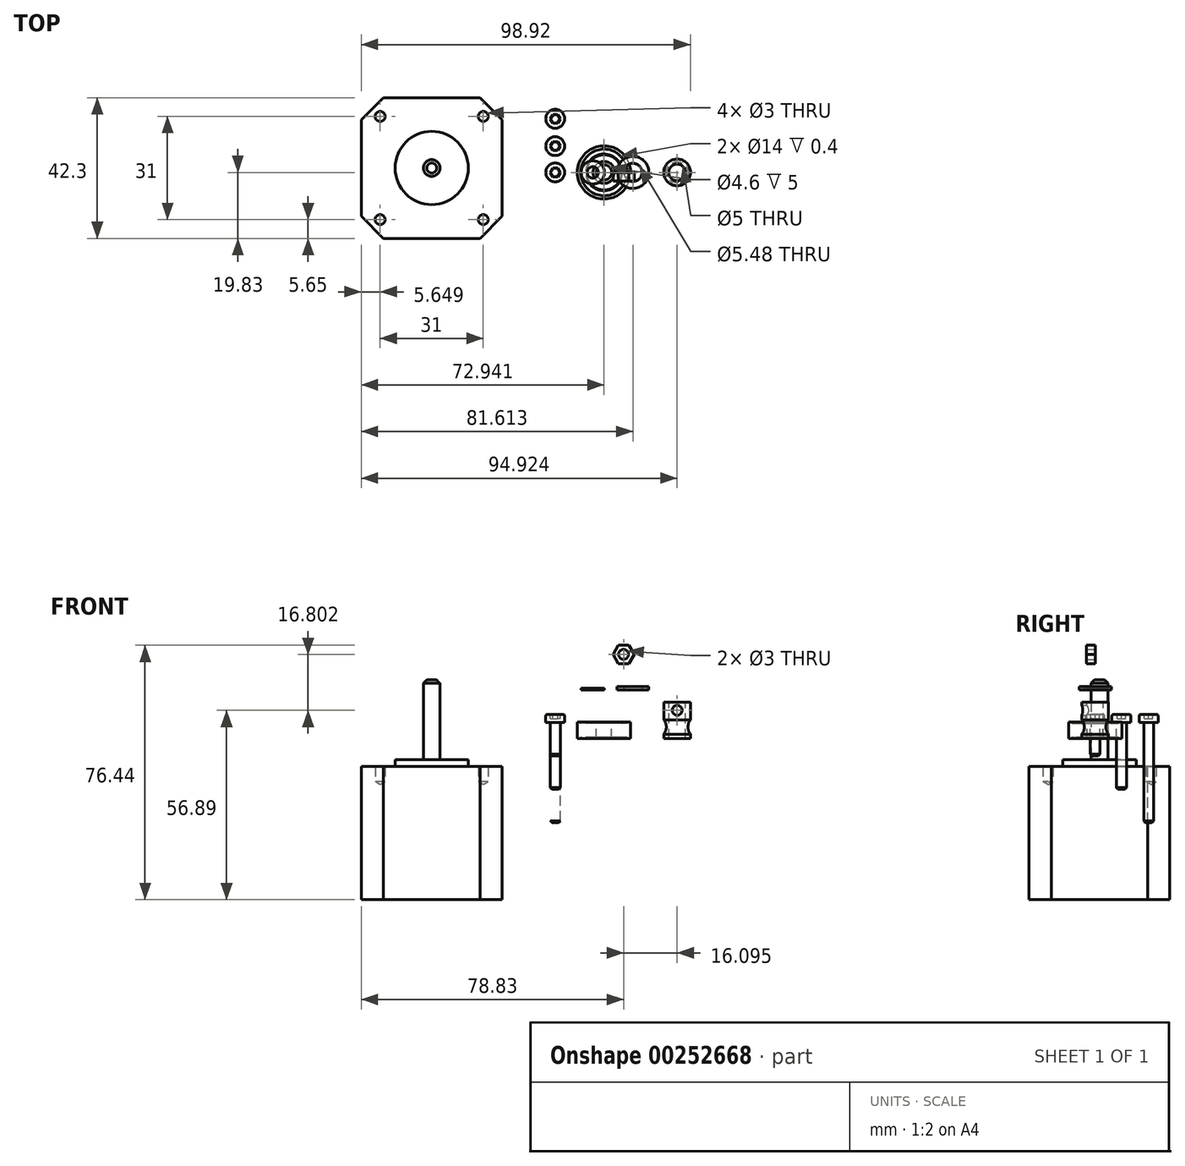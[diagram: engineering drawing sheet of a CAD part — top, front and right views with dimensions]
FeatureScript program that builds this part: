
annotation { "Feature Type Name" : "Feature", "Feature Type Description" : "" }
export const myFeature = defineFeature(function(context is Context, id is Id, definition is map)
    precondition{}
    {
        {
            var Q0;
            Q0=qCreatedBy(makeId("Front.planeOp"),FACE);
            var sketch = newSketch(context, id + "F0", { "sketchPlane" : qUnion([Q0])});
            skLineSegment(sketch, "E0.bottom", {"start": v(-24.66, 19.4) * mm, "end": v(-16.66, 19.4) * mm});
            skLineSegment(sketch, "E0.top", {"start": v(-24.66, 8.4) * mm, "end": v(-16.66, 8.4) * mm});
            skLineSegment(sketch, "E0.left", {"start": v(-24.66, 19.4) * mm, "end": v(-24.66, 8.4) * mm});
            skLineSegment(sketch, "E0.right", {"start": v(-16.66, 19.4) * mm, "end": v(-16.66, 8.4) * mm});
            skLineSegment(sketch, "E1", {"start": v(-20.66, 19.4) * mm, "end": v(-20.66, 8.4) * mm, "construction": true});
            skLineSegment(sketch, "E2", {"start": v(-23.16, 19.4) * mm, "end": v(-23.16, 8.4) * mm});
            skLineSegment(sketch, "E3", {"start": v(-18.16, 8.4) * mm, "end": v(-18.16, 19.4) * mm});
            skCircle(sketch, "E4", {"center": v(-27.4, 11.9) * mm, "radius": 3.5 * mm});
            skCircle(sketch, "E5", {"center": v(-20.66, 16.9) * mm, "radius": 1.5 * mm});
            skLineSegment(sketch, "E6", {"start": v(-34.64, 8.35) * mm, "end": v(-34.64, 13.35) * mm});
            skLineSegment(sketch, "E7", {"start": v(-34.64, 13.35) * mm, "end": v(-50.64, 13.35) * mm, "construction": true});
            skLineSegment(sketch, "E8", {"start": v(-50.64, 13.35) * mm, "end": v(-50.64, 8.35) * mm});
            skLineSegment(sketch, "E9", {"start": v(-50.64, 8.35) * mm, "end": v(-34.64, 8.35) * mm, "construction": true});
            skLineSegment(sketch, "E10", {"start": v(-44.94, 13.35) * mm, "end": v(-44.94, 8.35) * mm});
            skLineSegment(sketch, "E11", {"start": v(-39.94, 13.35) * mm, "end": v(-39.94, 8.35) * mm});
            skLineSegment(sketch, "E12", {"start": v(-42.64, 13.35) * mm, "end": v(-42.64, 8.35) * mm, "construction": true});
            skLineSegment(sketch, "E13", {"start": v(-44.94, 13.35) * mm, "end": v(-45.94, 13.35) * mm});
            skLineSegment(sketch, "E14", {"start": v(-45.94, 13.35) * mm, "end": v(-45.94, 13.15) * mm});
            skLineSegment(sketch, "E15", {"start": v(-45.94, 13.15) * mm, "end": v(-47.94, 13.15) * mm});
            skLineSegment(sketch, "E16", {"start": v(-47.94, 13.15) * mm, "end": v(-48.14, 12.95) * mm});
            skLineSegment(sketch, "E17", {"start": v(-48.14, 12.95) * mm, "end": v(-49.64, 12.95) * mm});
            skLineSegment(sketch, "E18", {"start": v(-49.64, 12.95) * mm, "end": v(-49.64, 13.35) * mm});
            skLineSegment(sketch, "E19", {"start": v(-49.64, 13.35) * mm, "end": v(-50.64, 13.35) * mm});
            skLineSegment(sketch, "E20", {"start": v(-50.64, 8.35) * mm, "end": v(-49.64, 8.35) * mm});
            skLineSegment(sketch, "E21", {"start": v(-49.64, 8.35) * mm, "end": v(-49.64, 8.75) * mm});
            skLineSegment(sketch, "E22", {"start": v(-49.64, 8.75) * mm, "end": v(-48.14, 8.75) * mm});
            skLineSegment(sketch, "E23", {"start": v(-48.14, 8.75) * mm, "end": v(-47.94, 8.55) * mm});
            skLineSegment(sketch, "E24", {"start": v(-47.94, 8.55) * mm, "end": v(-45.94, 8.55) * mm});
            skLineSegment(sketch, "E25", {"start": v(-45.94, 8.55) * mm, "end": v(-45.94, 8.35) * mm});
            skLineSegment(sketch, "E26", {"start": v(-45.94, 8.35) * mm, "end": v(-44.94, 8.35) * mm});
            skLineSegment(sketch, "E27.bottom", {"start": v(-49.5, 23.55) * mm, "end": v(-42.5, 23.55) * mm, "construction": true});
            skLineSegment(sketch, "E27.top", {"start": v(-49.5, 23.05) * mm, "end": v(-42.5, 23.05) * mm, "construction": true});
            skLineSegment(sketch, "E27.left", {"start": v(-49.5, 23.55) * mm, "end": v(-49.5, 23.05) * mm, "construction": true});
            skLineSegment(sketch, "E27.right", {"start": v(-42.5, 23.55) * mm, "end": v(-42.5, 23.05) * mm, "construction": true});
            skLineSegment(sketch, "E28", {"start": v(-46, 23.55) * mm, "end": v(-46, 23.05) * mm, "construction": true});
            skLineSegment(sketch, "E29.bottom", {"start": v(-49.5, 23.55) * mm, "end": v(-47.69, 23.55) * mm});
            skLineSegment(sketch, "E29.top", {"start": v(-49.5, 23.05) * mm, "end": v(-47.69, 23.05) * mm});
            skLineSegment(sketch, "E29.left", {"start": v(-49.5, 23.55) * mm, "end": v(-49.5, 23.05) * mm});
            skLineSegment(sketch, "E29.right", {"start": v(-47.69, 23.55) * mm, "end": v(-47.69, 23.05) * mm});
            skLineSegment(sketch, "E30", {"start": v(-60.14, 15.17) * mm, "end": v(-60.14, 13.17) * mm});
            skLineSegment(sketch, "E31", {"start": v(-60.14, 13.17) * mm, "end": v(-54.46, 13.17) * mm});
            skLineSegment(sketch, "E32", {"start": v(-54.46, 13.17) * mm, "end": v(-54.46, 15.17) * mm});
            skLineSegment(sketch, "E33", {"start": v(-54.96, 15.67) * mm, "end": v(-59.64, 15.67) * mm});
            skLineSegment(sketch, "E34", {"start": v(-57.3, 13.17) * mm, "end": v(-57.3, 3.17) * mm});
            skLineSegment(sketch, "E35", {"start": v(-58.8, 13.17) * mm, "end": v(-58.8, 3.17) * mm, "construction": true});
            skLineSegment(sketch, "E36", {"start": v(-58.8, 3.17) * mm, "end": v(-55.8, 3.17) * mm, "construction": true});
            skLineSegment(sketch, "E37", {"start": v(-55.8, 3.17) * mm, "end": v(-55.8, 13.17) * mm, "construction": true});
            skPoint(sketch, "E38.visualSharp", {"position": v(-60.14, 15.67) * mm});
            skArc(sketch, "E38.filletArc", {"start": v(-59.64, 15.67) * mm, "mid": v(-60, 15.53) * mm, "end": v(-60.14, 15.17) * mm});
            skPoint(sketch, "E39.visualSharp", {"position": v(-54.46, 15.67) * mm});
            skArc(sketch, "E39.filletArc", {"start": v(-54.46, 15.17) * mm, "mid": v(-54.6, 15.53) * mm, "end": v(-54.96, 15.67) * mm});
            skLineSegment(sketch, "E40", {"start": v(-58.8, 13.17) * mm, "end": v(-58.8, 3.17) * mm});
            skLineSegment(sketch, "E41", {"start": v(-58.8, 3.17) * mm, "end": v(-55.8, 3.17) * mm});
            skLineSegment(sketch, "E42", {"start": v(-55.8, 3.17) * mm, "end": v(-55.8, 13.17) * mm});
            skLineSegment(sketch, "E43", {"start": v(-57.3, 13.17) * mm, "end": v(-57.3, 15.67) * mm});
            skLineSegment(sketch, "E44", {"start": v(-38.79, 23.05) * mm, "end": v(-29.15, 23.05) * mm, "construction": true});
            skLineSegment(sketch, "E45", {"start": v(-29.15, 23.05) * mm, "end": v(-29.15, 24.05) * mm});
            skLineSegment(sketch, "E46", {"start": v(-29.15, 24.05) * mm, "end": v(-38.79, 24.05) * mm, "construction": true});
            skLineSegment(sketch, "E47", {"start": v(-38.79, 24.05) * mm, "end": v(-38.79, 23.05) * mm});
            skLineSegment(sketch, "E48", {"start": v(-33.97, 23.05) * mm, "end": v(-33.97, 24.05) * mm, "construction": true});
            skLineSegment(sketch, "E49", {"start": v(-36.7, 23.05) * mm, "end": v(-36.7, 24.05) * mm});
            skLineSegment(sketch, "E50", {"start": v(-36.7, 24.05) * mm, "end": v(-38.79, 24.05) * mm});
            skLineSegment(sketch, "E51", {"start": v(-36.7, 23.05) * mm, "end": v(-38.79, 23.05) * mm});
            skCircle(sketch, "E52.cCircle", {"center": v(-36.75, 33.7) * mm, "radius": 2.75 * mm, "construction": true});
            skLineSegment(sketch, "E52.0", {"start": v(-35.16, 30.94) * mm, "end": v(-38.34, 30.94) * mm});
            skLineSegment(sketch, "E52.1", {"start": v(-38.34, 30.94) * mm, "end": v(-39.93, 33.7) * mm});
            skLineSegment(sketch, "E52.2", {"start": v(-39.93, 33.7) * mm, "end": v(-38.34, 36.44) * mm});
            skLineSegment(sketch, "E52.3", {"start": v(-38.34, 36.44) * mm, "end": v(-35.16, 36.44) * mm});
            skLineSegment(sketch, "E52.4", {"start": v(-35.16, 36.44) * mm, "end": v(-33.57, 33.7) * mm});
            skLineSegment(sketch, "E52.5", {"start": v(-33.57, 33.7) * mm, "end": v(-35.16, 30.94) * mm});
            skPoint(sketch, "E52.0.midPoint", {"position": v(-36.75, 30.94) * mm});
            skCircle(sketch, "E53", {"center": v(-36.75, 33.7) * mm, "radius": 1.5 * mm});
            skSolve(sketch);
        }
        {
            var Q0;
            {var subQ8=sQuery(id+"F0.wireOp",EDGE,"E2");Q0=makeQuery(id+"F0.imprint","IMPRINT",FACE,{"disambiguationData":[TD([[makeQuery(id+"F0.imprint","IMPRINT",EDGE,{"derivedFrom":subQ8}),-1.0]])]});}
            var Q1;
            Q1=sQuery(id+"F0.wireOp",EDGE,"E1");
            revolve(context, id + "F1", {"entities" : qUnion([Q0]), "axis" : qUnion([Q1]), "revolveType" : RevolveType.FULL});
        }
        {
            var Q0;
            Q0=makeQuery(id+"F0.imprint","IMPRINT",FACE,{"disambiguationData":[TD([[makeQuery(id+"F0.imprint","IMPRINT",EDGE,{"derivedFrom":sQuery(id+"F0.wireOp",EDGE,"E5")}),1.0]])]});
            extrude(context, id + "F2", {"entities" : qUnion([Q0]), "operationType" : NewBodyOperationType.REMOVE, "depth" : 25 * mm});
        }
        {
            var Q0;
            Q0=makeQuery(id+"F0.imprint","IMPRINT",FACE,{"disambiguationData":[TD([[makeQuery(id+"F0.imprint","IMPRINT",EDGE,{"derivedFrom":sQuery(id+"F0.wireOp",EDGE,"E8")}),1.0]])]});
            var Q1;
            Q1=sQuery(id+"F0.wireOp",EDGE,"E12");
            revolve(context, id + "F3", {"entities" : qUnion([Q0]), "axis" : qUnion([Q1]), "revolveType" : RevolveType.FULL});
        }
        {
            var Q0;
            Q0=qCreatedBy(makeId("Top.planeOp"),FACE);
            var sketch = newSketch(context, id + "F4", { "sketchPlane" : qUnion([Q0])});
            skLineSegment(sketch, "E54.bottom", {"start": v(-115.58, 22.47) * mm, "end": v(-73.28, 22.47) * mm, "construction": true});
            skLineSegment(sketch, "E54.top", {"start": v(-115.58, -19.83) * mm, "end": v(-73.28, -19.83) * mm, "construction": true});
            skLineSegment(sketch, "E54.left", {"start": v(-115.58, 22.47) * mm, "end": v(-115.58, -19.83) * mm, "construction": true});
            skLineSegment(sketch, "E54.right", {"start": v(-73.28, 22.47) * mm, "end": v(-73.28, -19.83) * mm, "construction": true});
            skCircle(sketch, "E55", {"center": v(-94.43, 1.32) * mm, "radius": 2.5 * mm});
            skPoint(sketch, "E55.centerSnap0", {"position": v(-94.43, 22.47) * mm});
            skPoint(sketch, "E55.centerSnap1", {"position": v(-73.28, 1.32) * mm});
            skLineSegment(sketch, "E56", {"start": v(-115.58, 15.82) * mm, "end": v(-108.93, 22.47) * mm});
            skLineSegment(sketch, "E57", {"start": v(-108.93, 22.47) * mm, "end": v(-79.93, 22.47) * mm});
            skLineSegment(sketch, "E58", {"start": v(-73.28, 15.82) * mm, "end": v(-79.93, 22.47) * mm});
            skLineSegment(sketch, "E59", {"start": v(-73.28, 15.82) * mm, "end": v(-73.28, -13.18) * mm});
            skLineSegment(sketch, "E60", {"start": v(-73.28, -13.18) * mm, "end": v(-79.93, -19.83) * mm});
            skLineSegment(sketch, "E61", {"start": v(-79.93, -19.83) * mm, "end": v(-108.93, -19.83) * mm});
            skLineSegment(sketch, "E62", {"start": v(-108.93, -19.83) * mm, "end": v(-115.58, -13.18) * mm});
            skLineSegment(sketch, "E63", {"start": v(-115.58, -13.18) * mm, "end": v(-115.58, 15.82) * mm});
            skPoint(sketch, "E64", {"position": v(-109.93, 16.82) * mm});
            skPoint(sketch, "E65", {"position": v(-78.93, 16.82) * mm});
            skPoint(sketch, "E66", {"position": v(-78.93, -14.18) * mm});
            skPoint(sketch, "E67", {"position": v(-109.93, -14.18) * mm});
            skCircle(sketch, "E68", {"center": v(-94.43, 1.32) * mm, "radius": 11 * mm});
            skSolve(sketch);
        }
        {
            var Q0;
            Q0=makeQuery(id+"F4.imprint","IMPRINT",FACE,{"disambiguationData":[TD([[makeQuery(id+"F4.imprint","IMPRINT",EDGE,{"derivedFrom":sQuery(id+"F4.wireOp",EDGE,"E55")}),-1.0]])]});
            var Q1;
            Q1=makeQuery(id+"F4.imprint","IMPRINT",FACE,{"disambiguationData":[TD([[makeQuery(id+"F4.imprint","IMPRINT",EDGE,{"derivedFrom":sQuery(id+"F4.wireOp",EDGE,"E55")}),1.0]])]});
            extrude(context, id + "F5", {"entities" : qUnion([Q0, Q1]), "depth" : 2 * mm});
        }
        {
            var Q0;
            Q0=makeQuery(id+"F4.imprint","IMPRINT",FACE,{"disambiguationData":[TD([[makeQuery(id+"F4.imprint","IMPRINT",EDGE,{"derivedFrom":sQuery(id+"F4.wireOp",EDGE,"E55")}),1.0]])]});
            extrude(context, id + "F6", {"entities" : qUnion([Q0]), "operationType" : NewBodyOperationType.ADD, "depth" : 26 * mm});
        }
        {
            var Q0;
            Q0=makeQuery(id+"F4.imprint","IMPRINT",FACE,{"disambiguationData":[TD([[makeQuery(id+"F4.imprint","IMPRINT",EDGE,{"derivedFrom":sQuery(id+"F4.wireOp",EDGE,"E56")}),-1.0]])]});
            var Q1;
            Q1=makeQuery(id+"F4.imprint","IMPRINT",FACE,{"disambiguationData":[TD([[makeQuery(id+"F4.imprint","IMPRINT",EDGE,{"derivedFrom":sQuery(id+"F4.wireOp",EDGE,"E55")}),-1.0]])]});
            var Q2;
            Q2=makeQuery(id+"F4.imprint","IMPRINT",FACE,{"disambiguationData":[TD([[makeQuery(id+"F4.imprint","IMPRINT",EDGE,{"derivedFrom":sQuery(id+"F4.wireOp",EDGE,"E55")}),1.0]])]});
            extrude(context, id + "F7", {"entities" : qUnion([Q0, Q1, Q2]), "operationType" : NewBodyOperationType.ADD, "oppositeDirection" : true, "depth" : 40 * mm});
        }
        {
            var Q0;
            Q0=sQuery(id+"F4.wireOp",VERTEX,"E65");
            var Q1;
            Q1=sQuery(id+"F4.wireOp",VERTEX,"E66");
            var Q2;
            Q2=sQuery(id+"F4.wireOp",VERTEX,"E67");
            var Q3;
            Q3=sQuery(id+"F4.wireOp",VERTEX,"E64");
            var Q4;
            Q4=makeQuery(id+"F5.opExtrude","SWEPT_BODY",BODY,{"disambiguationData":[OSD([sQuery(id+"F4.wireOp",EDGE,"E68")])]});
            hole(context, id + "F8", {"style" : HoleStyle.SIMPLE, "endStyle" : HoleEndStyle.BLIND, "holeDiameter" : 3 * mm, "holeDepth" : 4.5 * mm, "locations" : qUnion([Q0, Q1, Q2, Q3]), "scope" : qUnion([Q4]), "startStyle" : HoleStartStyle.SKETCH});
        }
        {
            var Q0;
            Q0=makeQuery(id+"F6.opExtrude","CAP_EDGE",EDGE,{"disambiguationData":[OSD([sQuery(id+"F4.wireOp",EDGE,"E55")])],"isStart":false});
            chamfer(context, id + "F9", {"entities" : qUnion([Q0]), "width" : 1 * mm, "tangentPropagation" : true});
        }
        {
            var Q0;
            Q0=makeQuery(id+"F0.imprint","IMPRINT",FACE,{"disambiguationData":[TD([[makeQuery(id+"F0.imprint","IMPRINT",EDGE,{"derivedFrom":sQuery(id+"F0.wireOp",EDGE,"E29.bottom")}),-1.0]])]});
            var Q1;
            Q1=sQuery(id+"F0.wireOp",EDGE,"E28");
            revolve(context, id + "F10", {"entities" : qUnion([Q0]), "axis" : qUnion([Q1]), "revolveType" : RevolveType.FULL});
        }
        {
            var Q0;
            {var subQ3=sQuery(id+"F0.wireOp",EDGE,"E30");Q0=makeQuery(id+"F0.imprint","IMPRINT",FACE,{"disambiguationData":[TD([[makeQuery(id+"F0.imprint","IMPRINT",EDGE,{"derivedFrom":subQ3}),1.0]])]});}
            var Q1;
            {var subQ2=sQuery(id+"F0.wireOp",EDGE,"E34");Q1=makeQuery(id+"F0.imprint","IMPRINT",FACE,{"disambiguationData":[TD([[makeQuery(id+"F0.imprint","IMPRINT",EDGE,{"derivedFrom":subQ2}),-1.0]])]});}
            var Q2;
            Q2=sQuery(id+"F0.wireOp",EDGE,"E34");
            revolve(context, id + "F11", {"entities" : qUnion([Q0, Q1]), "axis" : qUnion([Q2]), "revolveType" : RevolveType.FULL});
        }
        {
            var Q0;
            Q0=makeQuery(id+"F11.opRevolve","SWEPT_FACE",FACE,{"disambiguationData":[OSD([sQuery(id+"F0.wireOp",EDGE,"E33")])]});
            var sketch = newSketch(context, id + "F12", { "sketchPlane" : qUnion([Q0])});
            skCircle(sketch, "E69.cCircle", {"center": v(-57.3, 0) * mm, "radius": 1.29 * mm, "construction": true});
            skLineSegment(sketch, "E69.0", {"start": v(-58.04, 1.29) * mm, "end": v(-56.55, 1.29) * mm});
            skLineSegment(sketch, "E69.1", {"start": v(-56.55, 1.29) * mm, "end": v(-55.8, 0) * mm});
            skLineSegment(sketch, "E69.2", {"start": v(-55.8, 0) * mm, "end": v(-56.55, -1.29) * mm});
            skLineSegment(sketch, "E69.3", {"start": v(-56.55, -1.29) * mm, "end": v(-58.04, -1.3) * mm});
            skLineSegment(sketch, "E69.4", {"start": v(-58.04, -1.29) * mm, "end": v(-58.79, 0) * mm});
            skLineSegment(sketch, "E69.5", {"start": v(-58.79, 0) * mm, "end": v(-58.04, 1.29) * mm});
            skPoint(sketch, "E69.0.midPoint", {"position": v(-57.3, 1.29) * mm});
            skSolve(sketch);
        }
        {
            var Q0;
            Q0=makeQuery(id+"F12.imprint","IMPRINT",FACE,{"disambiguationData":[TD([[makeQuery(id+"F12.imprint","IMPRINT",EDGE,{"derivedFrom":sQuery(id+"F12.wireOp",EDGE,"E69.0")}),-1.0]])]});
            extrude(context, id + "F13", {"entities" : qUnion([Q0]), "operationType" : NewBodyOperationType.REMOVE, "oppositeDirection" : true, "depth" : 1.3 * mm});
        }
        {
            var Q0;
            Q0=makeQuery(id+"F11.opRevolve","SWEPT_BODY",BODY,{"disambiguationData":[OSD([sQuery(id+"F0.wireOp",EDGE,"E30"),sQuery(id+"F0.wireOp",EDGE,"E31"),sQuery(id+"F0.wireOp",EDGE,"E33"),sQuery(id+"F0.wireOp",EDGE,"E34"),sQuery(id+"F0.wireOp",EDGE,"E38.filletArc"),sQuery(id+"F0.wireOp",EDGE,"E40"),sQuery(id+"F0.wireOp",EDGE,"jvlnToDY-RZYD-qugV-YEPu-XH3RUt0Xd54b"),sQuery(id+"F0.wireOp",EDGE,"E41"),sQuery(id+"F0.wireOp",EDGE,"E43")])]});
            transform(context, id + "F14", {"entities" : qUnion([Q0]), "transformType" : TransformType.TRANSLATION_3D, "dx" : 0 * mm, "dy" : 16.1 * mm, "dz" : 0 * mm, "makeCopy" : true});
        }
        {
            var Q0;
            Q0=makeQuery(id+"F14.opPattern","COPY",FACE,{"derivedFrom":makeQuery(id+"F11.opRevolve","SWEPT_FACE",FACE,{"disambiguationData":[OSD([sQuery(id+"F0.wireOp",EDGE,"E41")])]}),"instanceName":"1"});
            extrude(context, id + "F15", {"entities" : qUnion([Q0]), "operationType" : NewBodyOperationType.ADD, "depth" : 20 * mm});
        }
        {
            var Q0;
            Q0=makeQuery(id+"F0.imprint","IMPRINT",FACE,{"disambiguationData":[TD([[makeQuery(id+"F0.imprint","IMPRINT",EDGE,{"derivedFrom":sQuery(id+"F0.wireOp",EDGE,"E47")}),1.0]])]});
            var Q1;
            Q1=sQuery(id+"F0.wireOp",EDGE,"E48");
            revolve(context, id + "F16", {"entities" : qUnion([Q0]), "axis" : qUnion([Q1]), "revolveType" : RevolveType.FULL});
        }
        {
            var Q0;
            Q0=makeQuery(id+"F11.opRevolve","SWEPT_BODY",BODY,{"disambiguationData":[OSD([sQuery(id+"F0.wireOp",EDGE,"E30"),sQuery(id+"F0.wireOp",EDGE,"E31"),sQuery(id+"F0.wireOp",EDGE,"E33"),sQuery(id+"F0.wireOp",EDGE,"E34"),sQuery(id+"F0.wireOp",EDGE,"E38.filletArc"),sQuery(id+"F0.wireOp",EDGE,"E40"),sQuery(id+"F0.wireOp",EDGE,"E41"),sQuery(id+"F0.wireOp",EDGE,"E43")])]});
            transform(context, id + "F17", {"entities" : qUnion([Q0]), "transformType" : TransformType.TRANSLATION_3D, "dx" : 0 * mm, "dy" : 7.9 * mm, "dz" : 0 * mm, "makeCopy" : true});
        }
        {
            var Q0;
            Q0=makeQuery(id+"F17.opPattern","COPY",FACE,{"derivedFrom":makeQuery(id+"F11.opRevolve","SWEPT_FACE",FACE,{"disambiguationData":[OSD([sQuery(id+"F0.wireOp",EDGE,"E41")])]}),"instanceName":"1"});
            extrude(context, id + "F18", {"entities" : qUnion([Q0]), "operationType" : NewBodyOperationType.ADD, "depth" : 10 * mm});
        }
        {
            var Q0;
            Q0=makeQuery(id+"F15.opExtrude","CAP_FACE",FACE,{"disambiguationData":[OSD([sQuery(id+"F0.wireOp",EDGE,"E41")])],"isStart":false});
            var Q1;
            Q1=makeQuery(id+"F11.opRevolve","SWEPT_FACE",FACE,{"disambiguationData":[OSD([sQuery(id+"F0.wireOp",EDGE,"E41")])]});
            var Q2;
            Q2=makeQuery(id+"F18.opExtrude","CAP_EDGE",EDGE,{"disambiguationData":[OSD([sQuery(id+"F0.wireOp",EDGE,"E40"),sQuery(id+"F0.wireOp",EDGE,"E41")])],"isStart":false});
            chamfer(context, id + "F19", {"entities" : qUnion([Q0, Q1, Q2]), "width" : .5 * mm, "tangentPropagation" : true});
        }
        {
            var Q0;
            Q0=makeQuery(id+"F0.imprint","IMPRINT",FACE,{"disambiguationData":[TD([[makeQuery(id+"F0.imprint","IMPRINT",EDGE,{"derivedFrom":sQuery(id+"F0.wireOp",EDGE,"E52.0")}),-1.0]])]});
            extrude(context, id + "F20", {"entities" : qUnion([Q0]), "depth" : 2.6 * mm});
        }
    });
